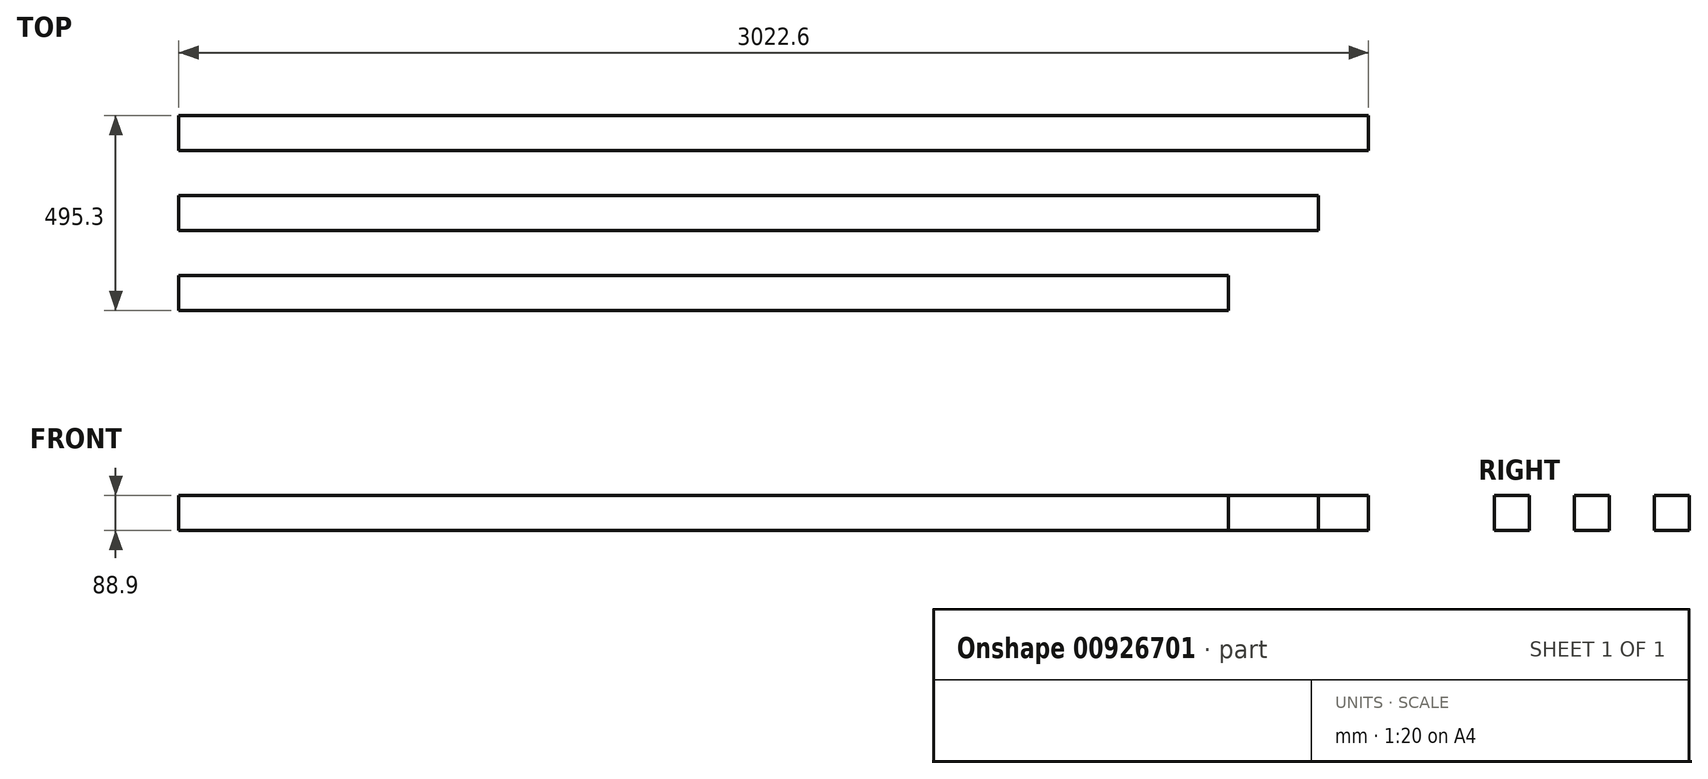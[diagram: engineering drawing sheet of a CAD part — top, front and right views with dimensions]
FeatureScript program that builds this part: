
annotation { "Feature Type Name" : "Feature", "Feature Type Description" : "" }
export const myFeature = defineFeature(function(context is Context, id is Id, definition is map)
    precondition{}
    {
        {
            var Q0;
            Q0=qCreatedBy(makeId("Right.planeOp"),FACE);
            var sketch = newSketch(context, id + "F0", { "sketchPlane" : qUnion([Q0])});
            skLineSegment(sketch, "E0.bottom", {"start": v(44.45, 44.45) * mm, "end": v(-44.45, 44.45) * mm});
            skLineSegment(sketch, "E0.top", {"start": v(44.45, -44.45) * mm, "end": v(-44.45, -44.45) * mm});
            skLineSegment(sketch, "E0.left", {"start": v(44.45, 44.45) * mm, "end": v(44.45, -44.45) * mm});
            skLineSegment(sketch, "E0.right", {"start": v(-44.45, 44.45) * mm, "end": v(-44.45, -44.45) * mm});
            skPoint(sketch, "E0.middle", {"position": v(0, 0) * mm});
            skSolve(sketch);
        }
        {
            var Q0;
            Q0=makeQuery(id+"F0.imprint","IMPRINT",FACE,{"disambiguationData":[TD([[makeQuery(id+"F0.imprint","IMPRINT",EDGE,{"derivedFrom":sQuery(id+"F0.wireOp",EDGE,"E0.bottom")}),1.0]])]});
            extrude(context, id + "F1", {"entities" : qUnion([Q0]), "depth" : 2667 * mm, "offsetDistance" : 25.4 * mm});
        }
        {
            var Q0;
            Q0=makeQuery(id+"F1.opExtrude","SWEPT_BODY",BODY,{"disambiguationData":[OSD([sQuery(id+"F0.wireOp",EDGE,"E0.bottom"),sQuery(id+"F0.wireOp",EDGE,"E0.top"),sQuery(id+"F0.wireOp",EDGE,"E0.left"),sQuery(id+"F0.wireOp",EDGE,"E0.right")])]});
            transform(context, id + "F2", {"entities" : qUnion([Q0]), "transformType" : TransformType.TRANSLATION_3D, "dx" : 0 * mm, "dy" : 203.2 * mm, "dz" : 0 * mm, "makeCopy" : true});
        }
        {
            var Q0;
            Q0=makeQuery(id+"F2.opPattern","COPY",FACE,{"derivedFrom":makeQuery(id+"F1.opExtrude","CAP_FACE",FACE,{"disambiguationData":[OSD([sQuery(id+"F0.wireOp",EDGE,"E0.bottom"),sQuery(id+"F0.wireOp",EDGE,"E0.top"),sQuery(id+"F0.wireOp",EDGE,"E0.left"),sQuery(id+"F0.wireOp",EDGE,"E0.right")])],"isStart":false}),"instanceName":"1"});
            extrude(context, id + "F3", {"entities" : qUnion([Q0]), "operationType" : NewBodyOperationType.ADD, "depth" : 228.6 * mm, "offsetDistance" : 25.4 * mm});
        }
        {
            var Q0;
            Q0=makeQuery(id+"F1.opExtrude","SWEPT_BODY",BODY,{"disambiguationData":[OSD([sQuery(id+"F0.wireOp",EDGE,"E0.bottom"),sQuery(id+"F0.wireOp",EDGE,"E0.top"),sQuery(id+"F0.wireOp",EDGE,"E0.left"),sQuery(id+"F0.wireOp",EDGE,"E0.right")])]});
            transform(context, id + "F4", {"entities" : qUnion([Q0]), "transformType" : TransformType.TRANSLATION_3D, "dx" : 0 * mm, "dy" : 406.4 * mm, "dz" : 0 * mm, "makeCopy" : true});
        }
        {
            var Q0;
            Q0=makeQuery(id+"F4.opPattern","COPY",FACE,{"derivedFrom":makeQuery(id+"F1.opExtrude","CAP_FACE",FACE,{"disambiguationData":[OSD([sQuery(id+"F0.wireOp",EDGE,"E0.bottom"),sQuery(id+"F0.wireOp",EDGE,"E0.top"),sQuery(id+"F0.wireOp",EDGE,"E0.left"),sQuery(id+"F0.wireOp",EDGE,"E0.right")])],"isStart":false}),"instanceName":"1"});
            extrude(context, id + "F5", {"entities" : qUnion([Q0]), "operationType" : NewBodyOperationType.ADD, "depth" : 355.6 * mm, "offsetDistance" : 25.4 * mm});
        }
    });
